# Revit family: Strainers 4111
name_source: partatom
category: Rohrzubehör
units: mm (PartAtom-declared; Revit-internal decimal feet)

## family parameters
Arbeitsebenenbasiert = Nein
Beim Laden mit Abzugskörper schneiden = Nein
Bemaßung runder Anschluss = Durchmesser verwenden
Gemeinsam genutzt = Nein
Immer vertikal = Ja
OmniClass-Nummer = 23.65.55.14
OmniClass-Titel = Valves for Liquid Services
Teiletyp = Unterbricht

## types (1)
- Strainers 4111
    Application = strainers are installed in pipes to protect the finely machined valve seats from particles.
field of application are building services, such as in heating or chilled water units for air conditioning in buildings.
EPDM sealings can be destroyed by organic hydro carbons, which are occurring in natural gas, mineral oil or lubricants.
    Body = casted, dezincification-resistant brass CC770S
    Closing plug = forged brass acc to. EN 12420, CW617N
    Hersteller = Herz-Armaturen GmbH
    Internal thread = acc. to ISO 228-1
    L03 = 15 mm
    L10 = 3.5 mm  [stored 0.0114829 ft]
    L12 = 0.8 mm
    Medium = heating water quality according to ÖNORM H5195 or VDI-Standard 2035.
the use of ethylene or propylene glycol in a mixing ratio 25- 50% is allowed.
please refer to manufacturers documentation when using ethylene glycol products for frost and corrosion protection.
HERZ ball valve for heating and chilled water is not suitable for usage of agressive medium (such as: acids, alkalis, combustible and explosive gases) because it can destroy sealing components.
    Plug seals = EPDM
    R03 = 9.5 mm
    R100 = 1 mm  [stored 0.00328084 ft]
    SCRNCODE = 05;15;02
    SCRNSEQ = AWI;AWI_TYP="1011";2
    SCTWCODE = 04;16;02
    SCTWSEQ = AW;SBT_TYP_AW="112";2
    Sieve = stainless steel, single, 1 4111 41-42: mashed perforation 0,5mm; 1 4111 14-18: meshed perforation 0.75mm
    URL = www.herzvalves.com
    W01 = 45.00°
    max. Operating temperature = 110 °C

note: [stored X ft] marks values corroborated as IEEE doubles in the binary element streams (Revit-internal decimal feet)
